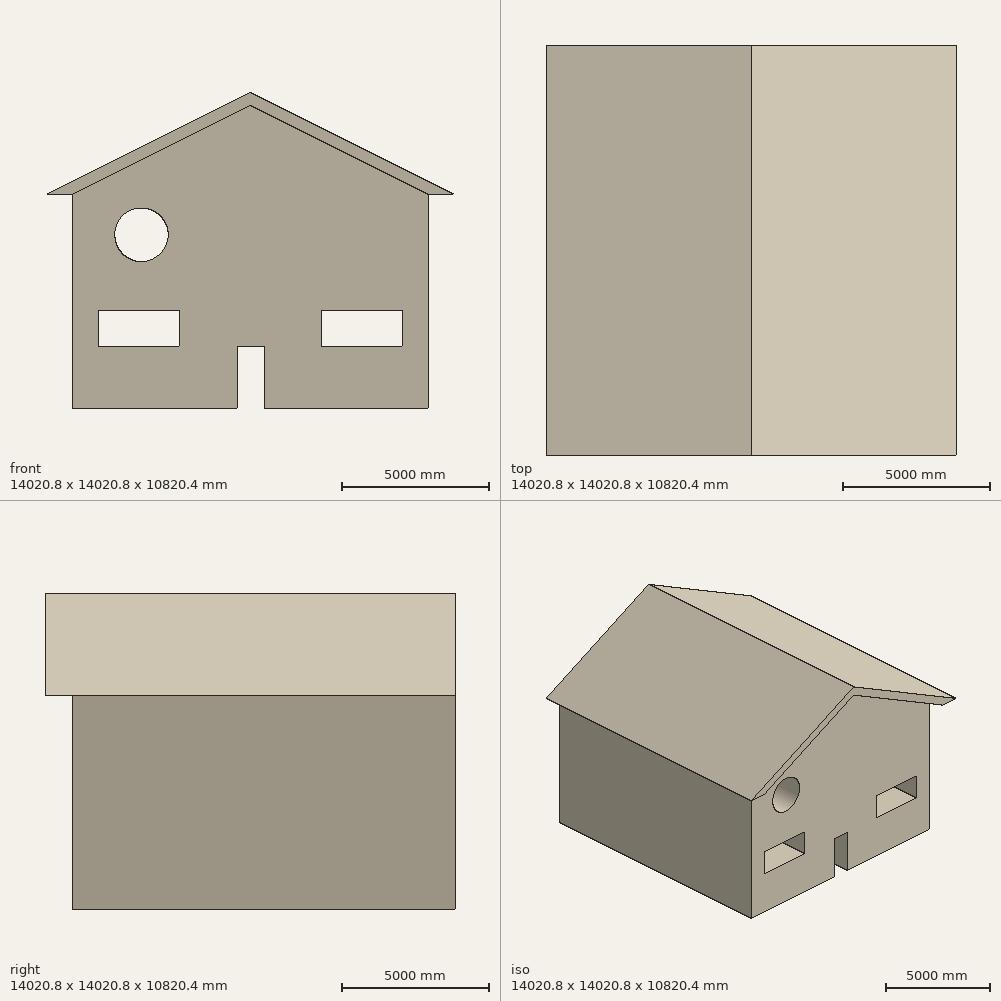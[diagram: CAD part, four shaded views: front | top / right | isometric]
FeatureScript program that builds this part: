
annotation { "Feature Type Name" : "Feature", "Feature Type Description" : "" }
export const myFeature = defineFeature(function(context is Context, id is Id, definition is map)
    precondition{}
    {
        {
            var Q0;
            Q0=qCreatedBy(makeId("Front.planeOp"),FACE);
            var sketch = newSketch(context, id + "F0", { "sketchPlane" : qUnion([Q0])});
            skLineSegment(sketch, "E0", {"start": v(0, 0) * mm, "end": v(-6096, 0) * mm});
            skLineSegment(sketch, "E1", {"start": v(0, 0) * mm, "end": v(6096, 0) * mm});
            skLineSegment(sketch, "E2", {"start": v(0, 0) * mm, "end": v(0, 3048) * mm, "construction": true});
            skLineSegment(sketch, "E3", {"start": v(0, 3048) * mm, "end": v(-6096, 0) * mm});
            skLineSegment(sketch, "E4", {"start": v(0, 3048) * mm, "end": v(6096, 0) * mm});
            skLineSegment(sketch, "E5", {"start": v(6096, 0) * mm, "end": v(7010.4, 0) * mm});
            skLineSegment(sketch, "E6", {"start": v(-6096, 0) * mm, "end": v(-7010.4, 0) * mm});
            skLineSegment(sketch, "E7", {"start": v(0, 3048) * mm, "end": v(0, 3505.2) * mm});
            skLineSegment(sketch, "E8", {"start": v(0, 3505.2) * mm, "end": v(-7010.4, 0) * mm});
            skLineSegment(sketch, "E9", {"start": v(0, 3505.2) * mm, "end": v(7010.4, 0) * mm});
            skLineSegment(sketch, "E10", {"start": v(-6096, 0) * mm, "end": v(-6096, -7315.2) * mm});
            skLineSegment(sketch, "E11", {"start": v(-6096, -7315.2) * mm, "end": v(6096, -7315.2) * mm});
            skLineSegment(sketch, "E12", {"start": v(6096, 0) * mm, "end": v(6096, -7315.2) * mm});
            skLineSegment(sketch, "E13", {"start": v(0, 0) * mm, "end": v(0, -7315.2) * mm, "construction": true});
            skLineSegment(sketch, "E14.bottom", {"start": v(-5181.6, -3962.4) * mm, "end": v(-2438.4, -3962.4) * mm});
            skLineSegment(sketch, "E14.top", {"start": v(-5181.6, -5181.6) * mm, "end": v(-2438.4, -5181.6) * mm});
            skLineSegment(sketch, "E14.left", {"start": v(-5181.6, -3962.4) * mm, "end": v(-5181.6, -5181.6) * mm});
            skLineSegment(sketch, "E14.right", {"start": v(-2438.4, -3962.4) * mm, "end": v(-2438.4, -5181.6) * mm});
            skLineSegment(sketch, "E15.bottom", {"start": v(2438.4, -3962.4) * mm, "end": v(5181.6, -3962.4) * mm});
            skLineSegment(sketch, "E15.top", {"start": v(2438.4, -5181.6) * mm, "end": v(5181.6, -5181.6) * mm});
            skLineSegment(sketch, "E15.left", {"start": v(2438.4, -3962.4) * mm, "end": v(2438.4, -5181.6) * mm});
            skLineSegment(sketch, "E15.right", {"start": v(5181.6, -3962.4) * mm, "end": v(5181.6, -5181.6) * mm});
            skLineSegment(sketch, "E16.bottom", {"start": v(-447.02, -7315.2) * mm, "end": v(467.38, -7315.2) * mm});
            skLineSegment(sketch, "E16.top", {"start": v(-447.02, -5181.6) * mm, "end": v(467.38, -5181.6) * mm});
            skLineSegment(sketch, "E16.left", {"start": v(-447.02, -7315.2) * mm, "end": v(-447.02, -5181.6) * mm});
            skLineSegment(sketch, "E16.right", {"start": v(467.38, -7315.2) * mm, "end": v(467.38, -5181.6) * mm});
            skCircle(sketch, "E17", {"center": v(-3726.04, -1372.21) * mm, "radius": 914.4 * mm});
            skSolve(sketch);
        }
        {
            var Q0;
            Q0=makeQuery(id+"F0.imprint","IMPRINT",FACE,{"disambiguationData":[TD([[makeQuery(id+"F0.imprint","IMPRINT",EDGE,{"derivedFrom":sQuery(id+"F0.wireOp",EDGE,"E3")}),-1.0]])]});
            var Q1;
            Q1=makeQuery(id+"F0.imprint","IMPRINT",FACE,{"disambiguationData":[TD([[makeQuery(id+"F0.imprint","IMPRINT",EDGE,{"derivedFrom":sQuery(id+"F0.wireOp",EDGE,"E4")}),1.0]])]});
            extrude(context, id + "F1", {"entities" : qUnion([Q0, Q1]), "depth" : 14020.8 * mm, "offsetDistance" : 30.48 * mm});
        }
        {
            var Q0;
            Q0=makeQuery(id+"F0.imprint","IMPRINT",FACE,{"disambiguationData":[TD([[makeQuery(id+"F0.imprint","IMPRINT",EDGE,{"derivedFrom":sQuery(id+"F0.wireOp",EDGE,"E0")}),-1.0]])]});
            extrude(context, id + "F2", {"entities" : qUnion([Q0]), "operationType" : NewBodyOperationType.ADD, "depth" : 13106.4 * mm, "offsetDistance" : 30.48 * mm});
        }
        {
            var Q0;
            Q0=makeQuery(id+"F0.imprint","IMPRINT",FACE,{"disambiguationData":[TD([[makeQuery(id+"F0.imprint","IMPRINT",EDGE,{"derivedFrom":sQuery(id+"F0.wireOp",EDGE,"E0")}),1.0]])]});
            extrude(context, id + "F3", {"entities" : qUnion([Q0]), "operationType" : NewBodyOperationType.ADD, "depth" : 13106.4 * mm, "offsetDistance" : 30.48 * mm});
        }
        {
            var Q0;
            Q0=sQuery(id+"F0.wireOp",EDGE,"E11");
            extrude(context, id + "F4", {"bodyType" : ToolBodyType.SURFACE, "surfaceEntities" : qUnion([Q0]), "depth" : 13106.4 * mm, "offsetDistance" : 30.48 * mm});
        }
    });
